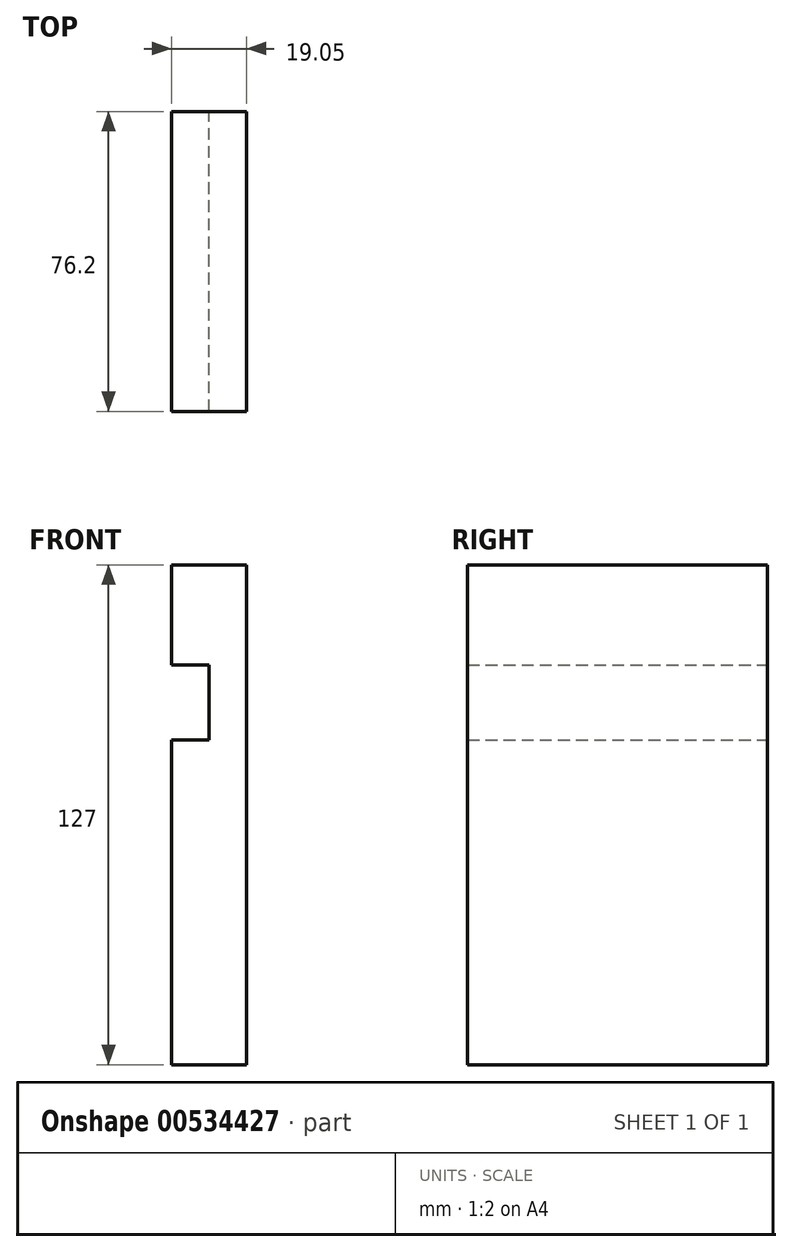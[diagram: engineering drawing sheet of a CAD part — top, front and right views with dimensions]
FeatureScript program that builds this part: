
annotation { "Feature Type Name" : "Feature", "Feature Type Description" : "" }
export const myFeature = defineFeature(function(context is Context, id is Id, definition is map)
    precondition{}
    {
        {
            var Q0;
            Q0=qCreatedBy(makeId("Front.planeOp"),FACE);
            var sketch = newSketch(context, id + "F0", { "sketchPlane" : qUnion([Q0])});
            skLineSegment(sketch, "E0", {"start": v(15.3, 55.68) * mm, "end": v(15.3, -71.32) * mm});
            skLineSegment(sketch, "E1", {"start": v(15.3, -71.32) * mm, "end": v(-3.75, -71.32) * mm});
            skLineSegment(sketch, "E2", {"start": v(15.3, 55.68) * mm, "end": v(-3.75, 55.68) * mm});
            skLineSegment(sketch, "E3", {"start": v(-3.75, 55.68) * mm, "end": v(-3.75, 30.28) * mm});
            skLineSegment(sketch, "E4", {"start": v(-3.75, 30.28) * mm, "end": v(5.77, 30.28) * mm});
            skLineSegment(sketch, "E5", {"start": v(5.77, 30.28) * mm, "end": v(5.77, 11.23) * mm});
            skLineSegment(sketch, "E6", {"start": v(5.77, 11.23) * mm, "end": v(-3.75, 11.23) * mm});
            skLineSegment(sketch, "E7", {"start": v(-3.75, 11.23) * mm, "end": v(-3.75, -71.32) * mm});
            skSolve(sketch);
        }
        {
            var Q0;
            Q0 = qSketchRegion(id + "F0", true);
            extrude(context, id + "F1", {"entities" : qUnion([Q0]), "depth" : 76.2 * mm, "offsetDistance" : 25.4 * mm});
        }
    });
